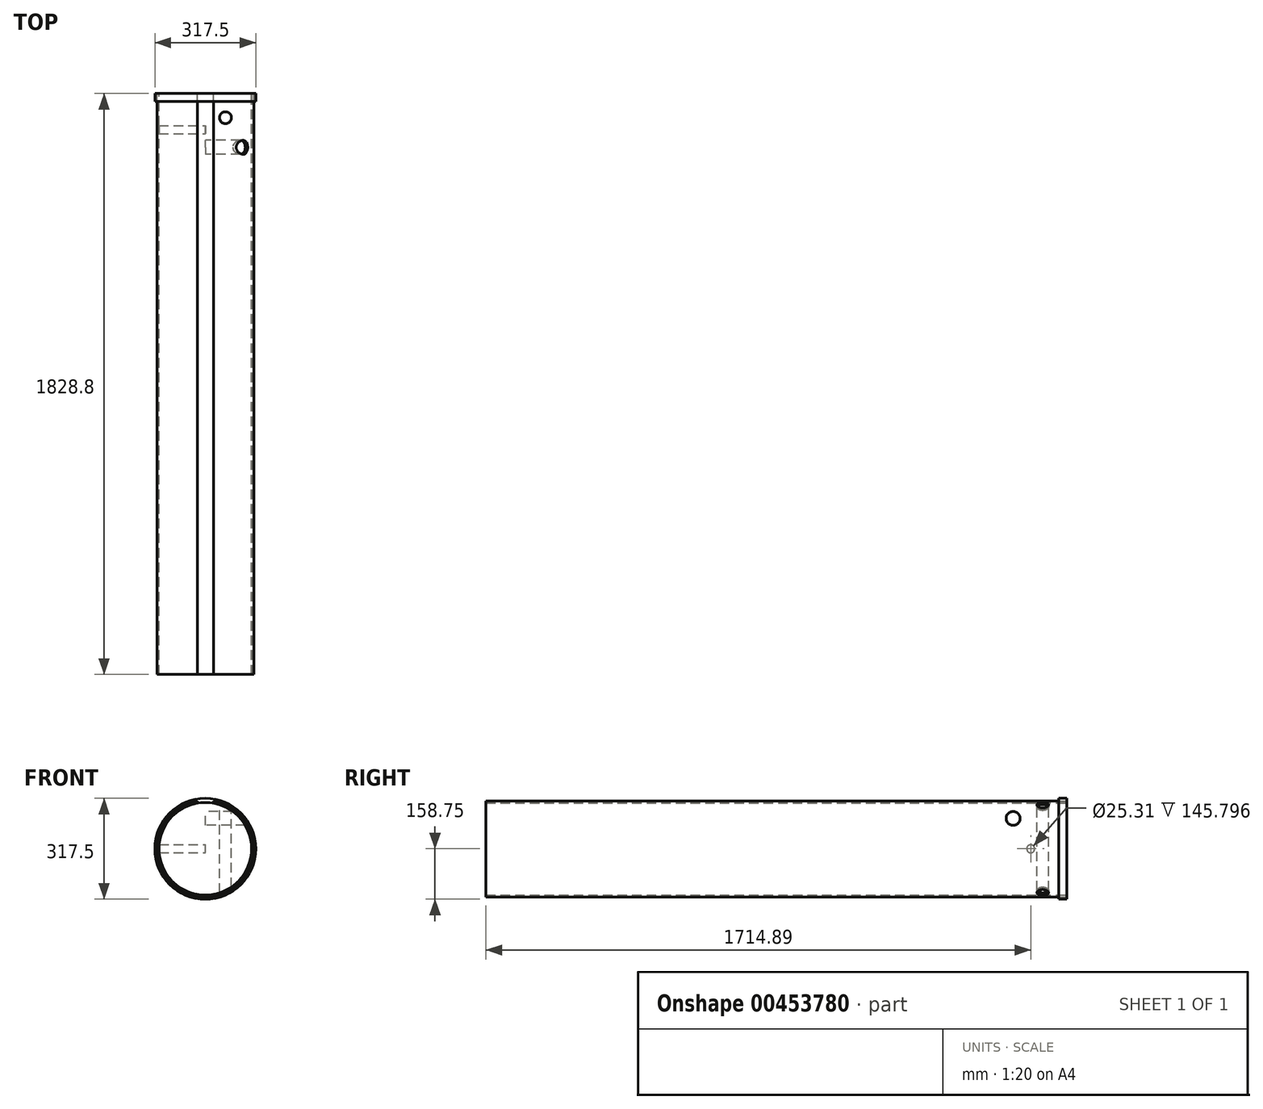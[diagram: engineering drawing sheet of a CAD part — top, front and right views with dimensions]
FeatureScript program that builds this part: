
annotation { "Feature Type Name" : "Feature", "Feature Type Description" : "" }
export const myFeature = defineFeature(function(context is Context, id is Id, definition is map)
    precondition{}
    {
        {
            var Q0;
            Q0=qCreatedBy(makeId("Front.planeOp"),FACE);
            var sketch = newSketch(context, id + "F0", { "sketchPlane" : qUnion([Q0])});
            skArc(sketch, "E0", {"start": v(-25.4, 150.27) * mm, "mid": v(0, -152.4) * mm, "end": v(25.4, 150.27) * mm});
            skArc(sketch, "E1", {"start": v(-25.4, 143.82) * mm, "mid": v(0, -146.05) * mm, "end": v(25.4, 143.82) * mm});
            skLineSegment(sketch, "E2.right", {"start": v(-25.4, 143.82) * mm, "end": v(-25.4, 150.27) * mm});
            skLineSegment(sketch, "E3.right", {"start": v(25.4, 143.82) * mm, "end": v(25.4, 150.27) * mm});
            skSolve(sketch);
        }
        {
            var Q0;
            Q0 = qSketchRegion(id + "F0", true);
            extrude(context, id + "F1", {"entities" : qUnion([Q0]), "depth" : 1828.8 * mm});
        }
        {
            var Q0;
            Q0=qCreatedBy(makeId("Front.planeOp"),FACE);
            var sketch = newSketch(context, id + "F2", { "sketchPlane" : qUnion([Q0])});
            skCircle(sketch, "E4", {"center": v(0, 0) * mm, "radius": 145.8 * mm});
            skSolve(sketch);
        }
        {
            var Q0;
            Q0 = qSketchRegion(id + "F2", true);
            extrude(context, id + "F3", {"entities" : qUnion([Q0]), "depth" : 1828.8 * mm});
        }
        {
            var Q0;
            Q0=qCreatedBy(makeId("Top.planeOp"),FACE);
            var sketch = newSketch(context, id + "F4", { "sketchPlane" : qUnion([Q0])});
            skCircle(sketch, "E5", {"center": v(63.47, -76.13) * mm, "radius": 18.7 * mm});
            skSolve(sketch);
        }
        {
            var Q0;
            Q0 = qSketchRegion(id + "F4", true);
            extrude(context, id + "F5", {"entities" : qUnion([Q0]), "operationType" : NewBodyOperationType.REMOVE, "endBound" : BoundingType.THROUGH_ALL, "oppositeDirection" : true, "depth" : 76.2 * mm, "hasSecondDirection" : true, "secondDirectionBound" : SecondDirectionBoundingType.THROUGH_ALL, "secondDirectionOppositeDirection" : false, "secondDirectionDepth" : 25.4 * mm});
        }
        {
            var Q0;
            Q0=qCreatedBy(makeId("Front.planeOp"),FACE);
            var sketch = newSketch(context, id + "F6", { "sketchPlane" : qUnion([Q0])});
            skCircle(sketch, "E6", {"center": v(0, 0) * mm, "radius": 158.75 * mm});
            skSolve(sketch);
        }
        {
            var Q0;
            Q0 = qSketchRegion(id + "F6", true);
            extrude(context, id + "F7", {"entities" : qUnion([Q0]), "depth" : 25.4 * mm});
        }
        {
            var Q0;
            Q0=qCreatedBy(makeId("Right.planeOp"),FACE);
            var sketch = newSketch(context, id + "F8", { "sketchPlane" : qUnion([Q0])});
            skCircle(sketch, "E7", {"center": v(-169.45, 95.59) * mm, "radius": 21.97 * mm});
            skSolve(sketch);
        }
        {
            var Q0;
            Q0 = qSketchRegion(id + "F8", true);
            extrude(context, id + "F9", {"entities" : qUnion([Q0]), "operationType" : NewBodyOperationType.REMOVE, "depth" : 254 * mm});
        }
        {
            var Q0;
            Q0=qCreatedBy(makeId("Right.planeOp"),FACE);
            var sketch = newSketch(context, id + "F10", { "sketchPlane" : qUnion([Q0])});
            skCircle(sketch, "E8", {"center": v(-113.91, 0) * mm, "radius": 12.66 * mm});
            skSolve(sketch);
        }
        {
            var Q0;
            Q0 = qSketchRegion(id + "F10", true);
            extrude(context, id + "F11", {"entities" : qUnion([Q0]), "operationType" : NewBodyOperationType.REMOVE, "oppositeDirection" : true, "depth" : 355.6 * mm});
        }
    });
